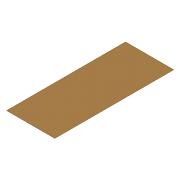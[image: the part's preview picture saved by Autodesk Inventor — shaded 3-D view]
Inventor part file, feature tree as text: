
AUTODESK INVENTOR PART (.ipt)
format: ipt  version: 2012 (Build 160160000, 160)  size: 71,168 bytes
history: native  units: in
note: dims shown in document units (in); Inventor stores cm internally (conversion verified against a paired STEP export)
features: extrude x1, sketch x1
ambient origin geometry x8: Origin, YZ Plane, XZ Plane, XY Plane, X Axis, Y Axis, Z Axis, Center Point
bodies: Solid1 (feature_tree)
feature tree (2):
  extrude  "Extrusion1"  Depth=360.0in
  sketch  "Sketch2"  dims[d0=888.0in d1=360.0in d2=0.25in d3=0.0in d4=444.0in d5=180.0in]
